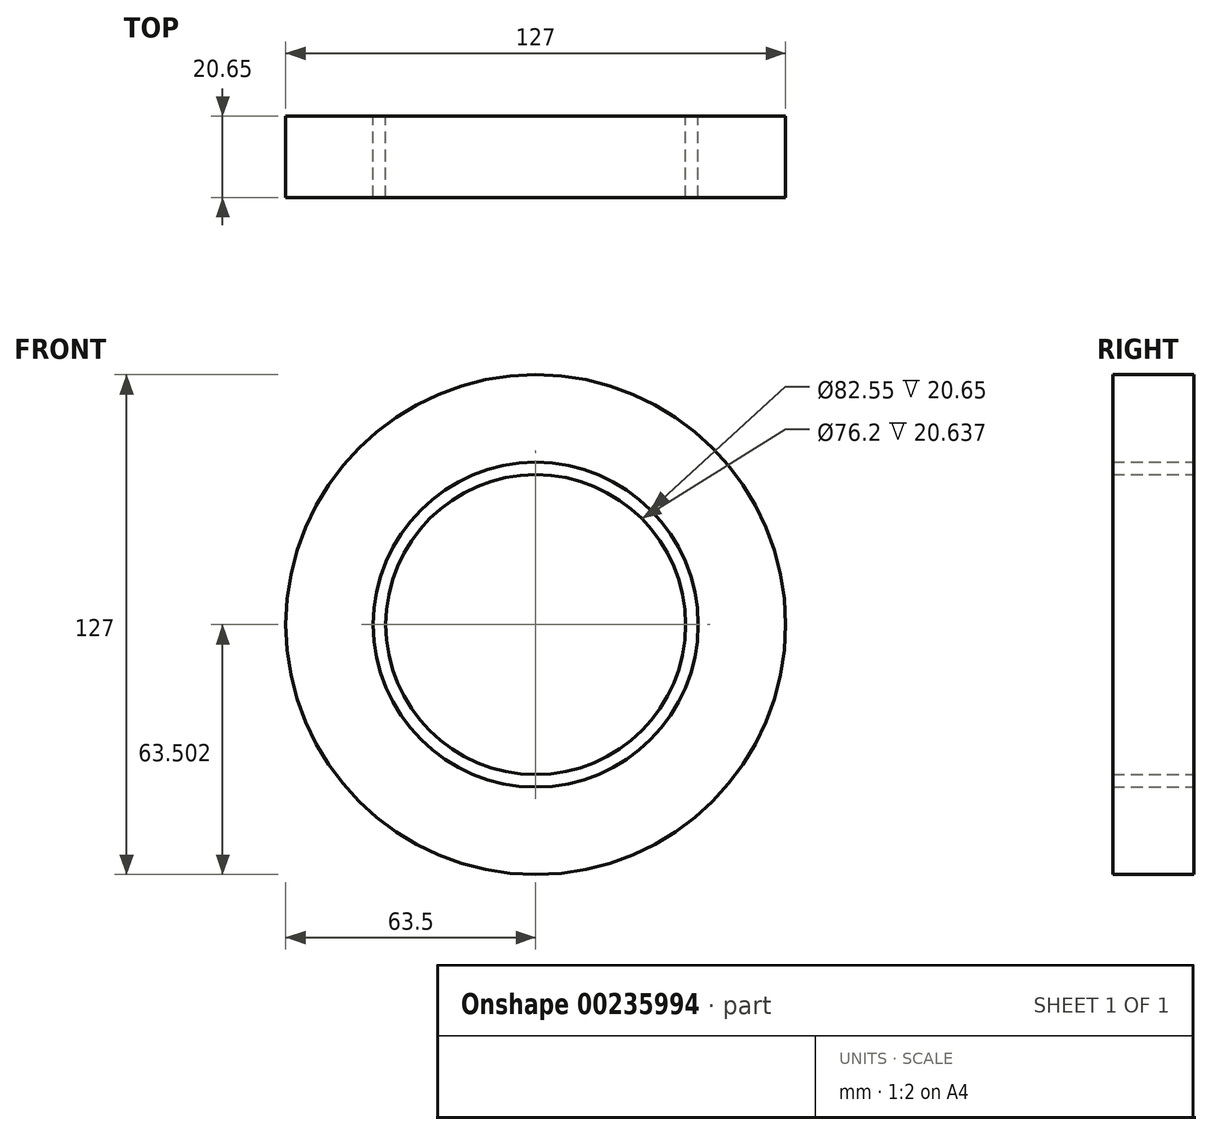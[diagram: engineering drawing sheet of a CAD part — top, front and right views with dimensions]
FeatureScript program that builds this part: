
annotation { "Feature Type Name" : "Feature", "Feature Type Description" : "" }
export const myFeature = defineFeature(function(context is Context, id is Id, definition is map)
    precondition{}
    {
        {
            var Q0;
            Q0=qCreatedBy(makeId("Front.planeOp"),FACE);
            var sketch = newSketch(context, id + "F0", { "sketchPlane" : qUnion([Q0])});
            skCircle(sketch, "E0", {"center": v(0, 10.58) * mm, "radius": 38.1 * mm});
            skCircle(sketch, "E1", {"center": v(0, 10.58) * mm, "radius": 41.28 * mm});
            skSolve(sketch);
        }
        {
            var Q0;
            Q0 = qSketchRegion(id + "F0", true);
            extrude(context, id + "F1", {"entities" : qUnion([Q0]), "depth" : 20.64 * mm});
        }
        {
            var Q0;
            Q0=qCreatedBy(makeId("Front.planeOp"),FACE);
            var sketch = newSketch(context, id + "F2", { "sketchPlane" : qUnion([Q0])});
            skCircle(sketch, "E2.0.0", {"center": v(0, 10.58) * mm, "radius": 41.28 * mm});
            skCircle(sketch, "E3.0", {"center": v(0, 10.58) * mm, "radius": 63.5 * mm});
            skSolve(sketch);
        }
        {
            var Q0;
            Q0 = qSketchRegion(id + "F2", true);
            extrude(context, id + "F3", {"entities" : qUnion([Q0]), "depth" : 20.65 * mm});
        }
    });
